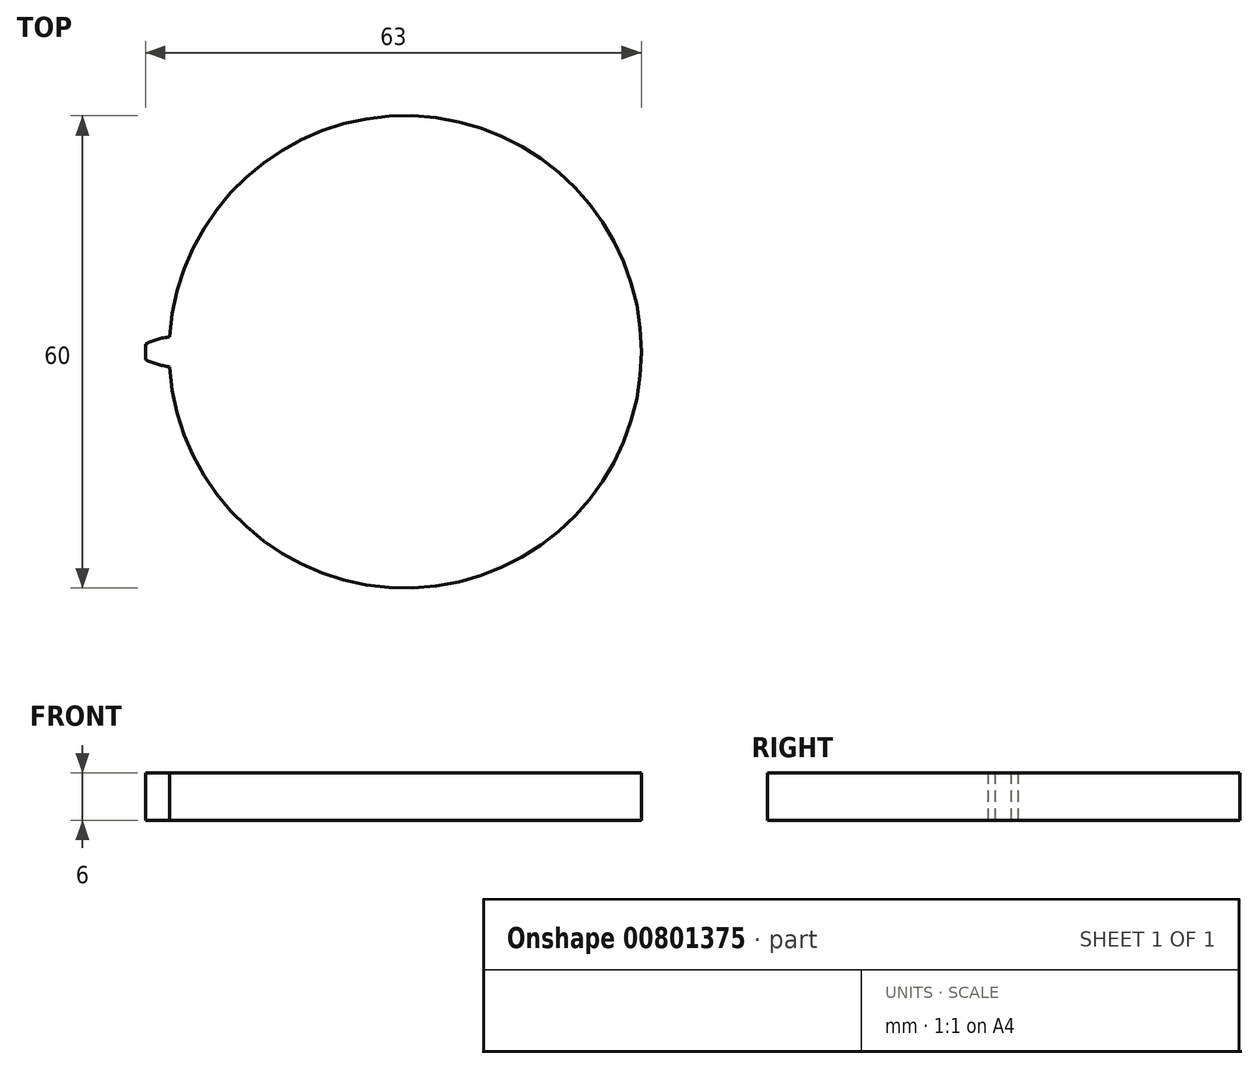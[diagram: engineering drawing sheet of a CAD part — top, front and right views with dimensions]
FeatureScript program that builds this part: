
annotation { "Feature Type Name" : "Feature", "Feature Type Description" : "" }
export const myFeature = defineFeature(function(context is Context, id is Id, definition is map)
    precondition{}
    {
        {
            var Q0;
            Q0=qCreatedBy(makeId("Top.planeOp"),FACE);
            var sketch = newSketch(context, id + "F0", { "sketchPlane" : qUnion([Q0])});
            skCircle(sketch, "E0", {"center": v(0, 0) * mm, "radius": 30 * mm});
            skSolve(sketch);
        }
        {
            var Q0;
            Q0=makeQuery(id+"F0.imprint","IMPRINT",FACE,{"disambiguationData":[TD([[makeQuery(id+"F0.imprint","IMPRINT",EDGE,{"derivedFrom":sQuery(id+"F0.wireOp",EDGE,"E0")}),1.0]])]});
            extrude(context, id + "F1", {"entities" : qUnion([Q0]), "depth" : 6 * mm, "offsetDistance" : 25 * mm});
        }
        {
            var Q0;
            Q0=makeQuery(id+"F1.opExtrude","CAP_FACE",FACE,{"disambiguationData":[OSD([sQuery(id+"F0.wireOp",EDGE,"E0")])],"isStart":false});
            var sketch = newSketch(context, id + "F2", { "sketchPlane" : qUnion([Q0])});
            skLineSegment(sketch, "E1", {"start": v(-33, -1) * mm, "end": v(-33, 1) * mm});
            skArc(sketch, "E2", {"start": v(-33, -1) * mm, "mid": v(-31.5, -1.57) * mm, "end": v(-29.94, -1.9) * mm});
            skArc(sketch, "E3", {"start": v(-29.94, 1.9) * mm, "mid": v(-30, 0) * mm, "end": v(-29.94, -1.9) * mm});
            skArc(sketch, "E4.trimOffspring", {"start": v(-29.94, 1.9) * mm, "mid": v(-31.5, 1.57) * mm, "end": v(-33, 1) * mm});
            skArc(sketch, "E5.trimOffspring", {"start": v(-24.32, -17.56) * mm, "mid": v(30, 0) * mm, "end": v(-24.32, 17.56) * mm});
            skSolve(sketch);
        }
        {
            var Q0;
            Q0=makeQuery(id+"F2.imprint","IMPRINT",FACE,{"disambiguationData":[TD([[makeQuery(id+"F2.imprint","IMPRINT",EDGE,{"derivedFrom":sQuery(id+"F2.wireOp",EDGE,"E1")}),-1.0]])]});
            extrude(context, id + "F3", {"entities" : qUnion([Q0]), "operationType" : NewBodyOperationType.ADD, "oppositeDirection" : true, "depth" : 6 * mm, "offsetDistance" : 25 * mm});
        }
    });
